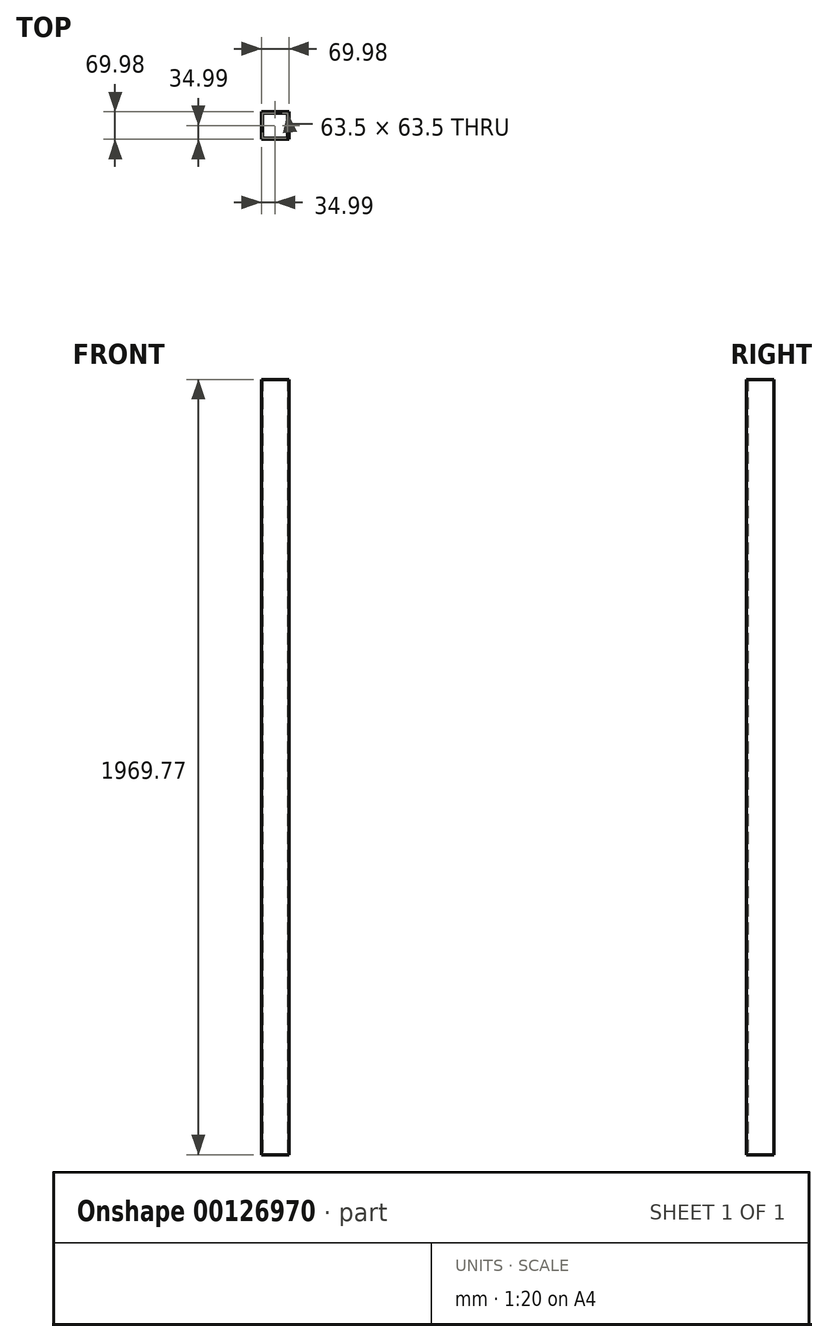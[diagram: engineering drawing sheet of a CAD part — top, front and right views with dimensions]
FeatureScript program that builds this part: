
annotation { "Feature Type Name" : "Feature", "Feature Type Description" : "" }
export const myFeature = defineFeature(function(context is Context, id is Id, definition is map)
    precondition{}
    {
        {
            var Q0;
            Q0=qCreatedBy(makeId("Top.planeOp"),FACE);
            var sketch = newSketch(context, id + "F0", { "sketchPlane" : qUnion([Q0])});
            skLineSegment(sketch, "E0.bottom", {"start": v(34.99, 34.99) * mm, "end": v(-34.99, 34.99) * mm});
            skLineSegment(sketch, "E0.top", {"start": v(34.99, -34.99) * mm, "end": v(-34.99, -34.99) * mm});
            skLineSegment(sketch, "E0.left", {"start": v(34.99, 34.99) * mm, "end": v(34.99, -34.99) * mm});
            skLineSegment(sketch, "E0.right", {"start": v(-34.99, 34.99) * mm, "end": v(-34.99, -34.99) * mm});
            skPoint(sketch, "E0.middle", {"position": v(0, 0) * mm});
            skLineSegment(sketch, "E1.bottom", {"start": v(31.75, 31.75) * mm, "end": v(-31.75, 31.75) * mm});
            skLineSegment(sketch, "E1.top", {"start": v(31.75, -31.75) * mm, "end": v(-31.75, -31.75) * mm});
            skLineSegment(sketch, "E1.left", {"start": v(31.75, 31.75) * mm, "end": v(31.75, -31.75) * mm});
            skLineSegment(sketch, "E1.right", {"start": v(-31.75, 31.75) * mm, "end": v(-31.75, -31.75) * mm});
            skSolve(sketch);
        }
        {
            var Q0;
            Q0=makeQuery(id+"F0.imprint","IMPRINT",FACE,{"disambiguationData":[TD([[makeQuery(id+"F0.imprint","IMPRINT",EDGE,{"derivedFrom":sQuery(id+"F0.wireOp",EDGE,"E0.bottom")}),1.0]])]});
            extrude(context, id + "F1", {"entities" : qUnion([Q0]), "depth" : 1969.77 * mm});
        }
    });
